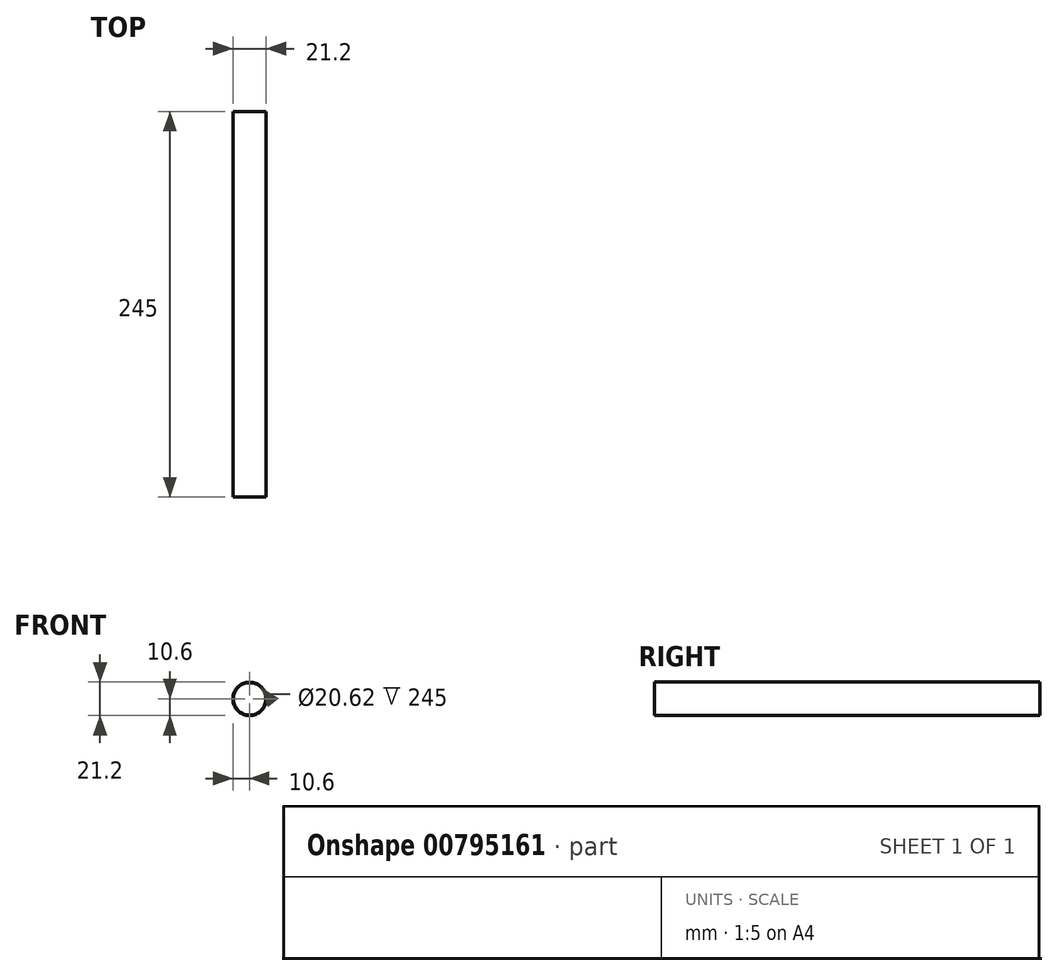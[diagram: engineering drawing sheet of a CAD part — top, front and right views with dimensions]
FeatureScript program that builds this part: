
annotation { "Feature Type Name" : "Feature", "Feature Type Description" : "" }
export const myFeature = defineFeature(function(context is Context, id is Id, definition is map)
    precondition{}
    {
        {
            var Q0;
            Q0=qCreatedBy(makeId("Front.planeOp"),FACE);
            var sketch = newSketch(context, id + "F0", { "sketchPlane" : qUnion([Q0])});
            skCircle(sketch, "E0", {"center": v(0, 0) * mm, "radius": 10.6 * mm});
            skCircle(sketch, "E1", {"center": v(0, 0) * mm, "radius": 10.31 * mm});
            skSolve(sketch);
        }
        {
            var Q0;
            Q0=makeQuery(id+"F0.imprint","IMPRINT",FACE,{"disambiguationData":[TD([[makeQuery(id+"F0.imprint","IMPRINT",EDGE,{"derivedFrom":sQuery(id+"F0.wireOp",EDGE,"E0")}),1.0]])]});
            extrude(context, id + "F1", {"entities" : qUnion([Q0]), "depth" : 245 * mm, "offsetDistance" : 25 * mm});
        }
    });
